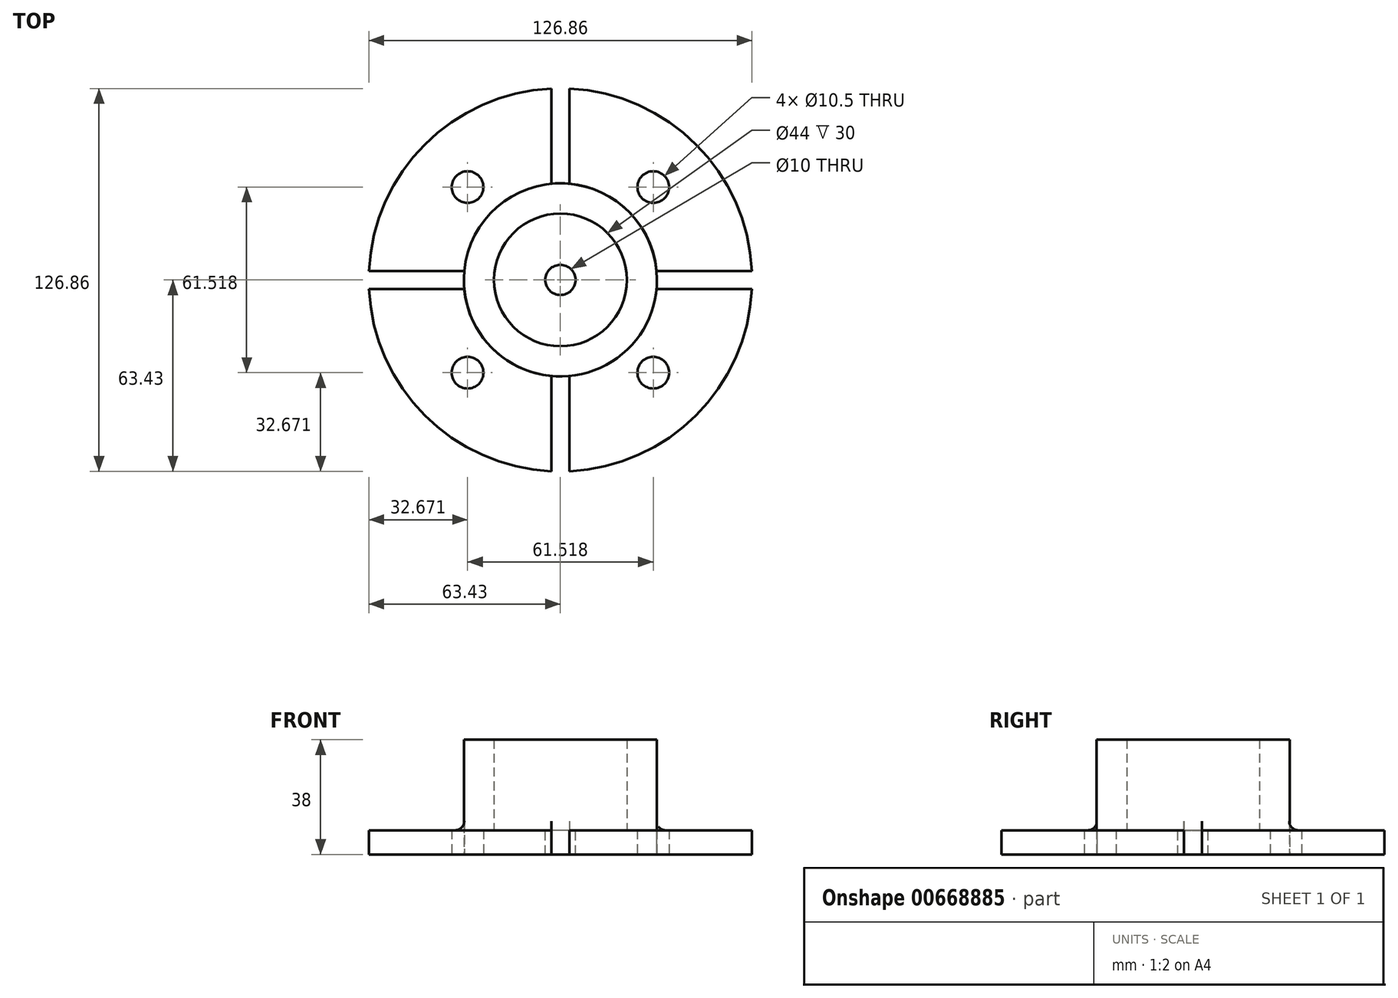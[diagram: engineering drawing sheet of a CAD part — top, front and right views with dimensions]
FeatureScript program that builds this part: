
annotation { "Feature Type Name" : "Feature", "Feature Type Description" : "" }
export const myFeature = defineFeature(function(context is Context, id is Id, definition is map)
    precondition{}
    {
        {
            var Q0;
            Q0=qCreatedBy(makeId("Top.planeOp"),FACE);
            var sketch = newSketch(context, id + "F0", { "sketchPlane" : qUnion([Q0])});
            skCircle(sketch, "E0", {"center": v(0, 0) * mm, "radius": 32 * mm});
            skArc(sketch, "E1", {"start": v(-63.43, -3) * mm, "mid": v(-44.9, -44.9) * mm, "end": v(-3, -63.43) * mm});
            skCircle(sketch, "E2", {"center": v(30.76, 30.76) * mm, "radius": 5.25 * mm});
            skCircle(sketch, "E3", {"center": v(-30.76, 30.76) * mm, "radius": 5.25 * mm});
            skCircle(sketch, "E4", {"center": v(-30.76, -30.76) * mm, "radius": 5.25 * mm});
            skCircle(sketch, "E5", {"center": v(30.76, -30.76) * mm, "radius": 5.25 * mm});
            skLineSegment(sketch, "E6.left", {"start": v(-3, -63.43) * mm, "end": v(-3, -31.86) * mm});
            skLineSegment(sketch, "E6.right", {"start": v(3, -63.43) * mm, "end": v(3, -31.86) * mm});
            skPoint(sketch, "E6.middle", {"position": v(0, -32) * mm});
            skPoint(sketch, "E7.orphan", {"position": v(-3, -0.57) * mm});
            skPoint(sketch, "E8.orphan", {"position": v(3, -0.57) * mm});
            skLineSegment(sketch, "E9.1.0", {"start": v(63.43, 3) * mm, "end": v(31.86, 3) * mm});
            skLineSegment(sketch, "E9.1.1", {"start": v(63.43, -3) * mm, "end": v(31.86, -3) * mm});
            skLineSegment(sketch, "E9.2.0", {"start": v(-3, 63.43) * mm, "end": v(-3, 31.86) * mm});
            skLineSegment(sketch, "E9.2.1", {"start": v(3, 63.43) * mm, "end": v(3, 31.86) * mm});
            skLineSegment(sketch, "E9.3.0", {"start": v(-63.43, -3) * mm, "end": v(-31.86, -3) * mm});
            skLineSegment(sketch, "E9.3.1", {"start": v(-63.43, 3) * mm, "end": v(-31.86, 3) * mm});
            skArc(sketch, "E10.trimOffspring", {"start": v(-3, 63.43) * mm, "mid": v(-44.9, 44.9) * mm, "end": v(-63.43, 3) * mm});
            skArc(sketch, "E11.trimOffspring", {"start": v(63.43, 3) * mm, "mid": v(44.9, 44.9) * mm, "end": v(3, 63.43) * mm});
            skArc(sketch, "E12.trimOffspring", {"start": v(3, -63.43) * mm, "mid": v(44.9, -44.9) * mm, "end": v(63.43, -3) * mm});
            skSolve(sketch);
        }
        {
            var Q0;
            Q0=makeQuery(id+"F0.imprint","IMPRINT",FACE,{"disambiguationData":[TD([[makeQuery(id+"F0.imprint","IMPRINT",EDGE,{"derivedFrom":sQuery(id+"F0.wireOp",EDGE,"E0")}),-1.0]])]});
            var Q1;
            Q1=makeQuery(id+"F0.imprint","IMPRINT",FACE,{"disambiguationData":[TD([[makeQuery(id+"F0.imprint","IMPRINT",EDGE,{"derivedFrom":sQuery(id+"F0.wireOp",EDGE,"E2")}),-1.0]])]});
            var Q2;
            Q2=makeQuery(id+"F0.imprint","IMPRINT",FACE,{"disambiguationData":[TD([[makeQuery(id+"F0.imprint","IMPRINT",EDGE,{"derivedFrom":sQuery(id+"F0.wireOp",EDGE,"E3")}),-1.0]])]});
            var Q3;
            Q3=makeQuery(id+"F0.imprint","IMPRINT",FACE,{"disambiguationData":[TD([[makeQuery(id+"F0.imprint","IMPRINT",EDGE,{"derivedFrom":sQuery(id+"F0.wireOp",EDGE,"E1")}),1.0]])]});
            var Q4;
            Q4=makeQuery(id+"F0.imprint","IMPRINT",FACE,{"disambiguationData":[TD([[makeQuery(id+"F0.imprint","IMPRINT",EDGE,{"derivedFrom":sQuery(id+"F0.wireOp",EDGE,"E5")}),-1.0]])]});
            var Q5;
            {var subQ0=sQuery(id+"F0.wireOp",EDGE,"E0");var subQ5=makeQuery(id+"F0.imprint","INTERSECT",VERTEX,{"derivedFrom":[subQ0,sQuery(id+"F0.wireOp",EDGE,"E9.1.0")]});Q5=makeQuery(id+"F0.imprint","IMPRINT",FACE,{"disambiguationData":[TD([[makeQuery(id+"F0.imprint","IMPRINT",EDGE,{"disambiguationData":[TD([[subQ5,-1.0]])],"derivedFrom":subQ0}),1.0]])]});}
            extrude(context, id + "F1", {"entities" : qUnion([Q0, Q1, Q2, Q3, Q4, Q5]), "flatOperationType" : FlatOperationType.REMOVE, "depth" : 8 * mm, "offsetDistance" : 25 * mm, "domain" : OperationDomain.MODEL});
        }
        {
            var Q0;
            Q0=makeQuery(id+"F1.opExtrude","CAP_FACE",FACE,{"disambiguationData":[OSD([sQuery(id+"F0.wireOp",EDGE,"E0"),sQuery(id+"F0.wireOp",EDGE,"E1"),sQuery(id+"F0.wireOp",EDGE,"E2"),sQuery(id+"F0.wireOp",EDGE,"E3"),sQuery(id+"F0.wireOp",EDGE,"E4"),sQuery(id+"F0.wireOp",EDGE,"E5")])],"isStart":false});
            var sketch = newSketch(context, id + "F2", { "sketchPlane" : qUnion([Q0])});
            skCircle(sketch, "E13", {"center": v(0, 0) * mm, "radius": 22 * mm});
            skCircle(sketch, "E14", {"center": v(0, 0) * mm, "radius": 32 * mm});
            skSolve(sketch);
        }
        {
            var Q0;
            Q0 = qSketchRegion(id + "F2", true);
            extrude(context, id + "F3", {"entities" : qUnion([Q0]), "operationType" : NewBodyOperationType.ADD, "flatOperationType" : FlatOperationType.REMOVE, "depth" : 30 * mm, "offsetDistance" : 25 * mm, "domain" : OperationDomain.MODEL});
        }
        {
            var Q0;
            {var subQ0=sQuery(id+"F0.wireOp",EDGE,"E6.left");var subQ3=sQuery(id+"F2.wireOp",EDGE,"E14");Q0=makeQuery(id+"F3.boolean.opBoolean","SPLIT",EDGE,{"disambiguationData":[TD([makeQuery(id+"F1.opExtrude","SWEPT_FACE",FACE,{"disambiguationData":[OSD([subQ0])]})])],"derivedFrom":makeQuery(id+"F3.opExtrude","CAP_EDGE",EDGE,{"disambiguationData":[OSD([subQ3])],"isStart":true})});}
            var Q1;
            {var subQ3=sQuery(id+"F0.wireOp",EDGE,"E9.2.0");var subQ4=sQuery(id+"F2.wireOp",EDGE,"E14");Q1=makeQuery(id+"F3.boolean.opBoolean","SPLIT",EDGE,{"disambiguationData":[TD([makeQuery(id+"F1.opExtrude","SWEPT_FACE",FACE,{"disambiguationData":[OSD([subQ3])]})])],"derivedFrom":makeQuery(id+"F3.opExtrude","CAP_EDGE",EDGE,{"disambiguationData":[OSD([subQ4])],"isStart":true})});}
            var Q2;
            {var subQ2=sQuery(id+"F0.wireOp",EDGE,"E6.right");var subQ3=sQuery(id+"F2.wireOp",EDGE,"E14");Q2=makeQuery(id+"F3.boolean.opBoolean","SPLIT",EDGE,{"disambiguationData":[TD([makeQuery(id+"F1.opExtrude","SWEPT_FACE",FACE,{"disambiguationData":[OSD([subQ2])]})])],"derivedFrom":makeQuery(id+"F3.opExtrude","CAP_EDGE",EDGE,{"disambiguationData":[OSD([subQ3])],"isStart":true})});}
            var Q3;
            {var subQ3=sQuery(id+"F2.wireOp",EDGE,"E14");var subQ9=sQuery(id+"F0.wireOp",EDGE,"E9.1.0");Q3=makeQuery(id+"F3.boolean.opBoolean","SPLIT",EDGE,{"disambiguationData":[TD([makeQuery(id+"F1.opExtrude","SWEPT_FACE",FACE,{"disambiguationData":[OSD([subQ9])]})])],"derivedFrom":makeQuery(id+"F3.opExtrude","CAP_EDGE",EDGE,{"disambiguationData":[OSD([subQ3])],"isStart":true})});}
            fillet(context, id + "F4", {"entities" : qUnion([Q0, Q1, Q2, Q3]), "radius" : 3 * mm, "tangentPropagation" : true, "defaultsChanged" : false, "vertexSettings" : [], "allowEdgeOverflow" : false});
        }
        {
            var Q0;
            Q0=makeQuery(id+"F3.boolean.opBoolean","SPLIT",FACE,{"disambiguationData":[TD([makeQuery(id+"F3.opExtrude","SWEPT_FACE",FACE,{"disambiguationData":[OSD([sQuery(id+"F2.wireOp",EDGE,"E13")])]})])],"derivedFrom":makeQuery(id+"F1.opExtrude","CAP_FACE",FACE,{"disambiguationData":[OSD([sQuery(id+"F0.wireOp",EDGE,"E0"),sQuery(id+"F0.wireOp",EDGE,"E1"),sQuery(id+"F0.wireOp",EDGE,"E2"),sQuery(id+"F0.wireOp",EDGE,"E3"),sQuery(id+"F0.wireOp",EDGE,"E4"),sQuery(id+"F0.wireOp",EDGE,"E5"),sQuery(id+"F0.wireOp",EDGE,"E6.left"),sQuery(id+"F0.wireOp",EDGE,"E6.right"),sQuery(id+"F0.wireOp",EDGE,"E9.1.0"),sQuery(id+"F0.wireOp",EDGE,"E9.1.1"),sQuery(id+"F0.wireOp",EDGE,"E9.2.0"),sQuery(id+"F0.wireOp",EDGE,"E9.2.1"),sQuery(id+"F0.wireOp",EDGE,"E9.3.0"),sQuery(id+"F0.wireOp",EDGE,"E9.3.1"),sQuery(id+"F0.wireOp",EDGE,"E10.trimOffspring"),sQuery(id+"F0.wireOp",EDGE,"E11.trimOffspring"),sQuery(id+"F0.wireOp",EDGE,"E12.trimOffspring")])],"isStart":false})});
            var sketch = newSketch(context, id + "F5", { "sketchPlane" : qUnion([Q0])});
            skCircle(sketch, "E15", {"center": v(0, 0) * mm, "radius": 22 * mm});
            skCircle(sketch, "E16", {"center": v(0, 0) * mm, "radius": 5 * mm});
            skSolve(sketch);
        }
        {
            var Q0;
            Q0=makeQuery(id+"F5.imprint","IMPRINT",FACE,{"disambiguationData":[TD([[makeQuery(id+"F5.imprint","IMPRINT",EDGE,{"derivedFrom":sQuery(id+"F5.wireOp",EDGE,"E16")}),1.0]])]});
            var Q1;
            Q1=makeQuery(id+"F5.imprint","IMPRINT",FACE,{"disambiguationData":[TD([[makeQuery(id+"F5.imprint","IMPRINT",EDGE,{"derivedFrom":sQuery(id+"F5.wireOp",EDGE,"E16")}),1.0]])]});
            extrude(context, id + "F6", {"entities" : qUnion([Q0, Q1]), "operationType" : NewBodyOperationType.REMOVE, "oppositeDirection" : true, "depth" : 19.3 * mm, "offsetDistance" : 25 * mm});
        }
    });
